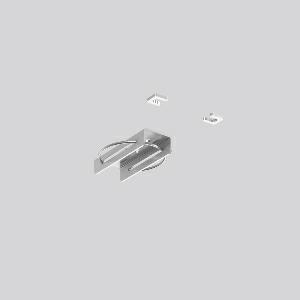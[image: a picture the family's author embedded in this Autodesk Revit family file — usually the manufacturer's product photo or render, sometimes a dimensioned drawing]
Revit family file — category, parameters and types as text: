
# Revit family: linedo_decke_adapter_982580_010_77cd
name_source: partatom
category: Lighting Fixtures
units: mm (PartAtom-declared; Revit-internal decimal feet)

## family parameters
Cut with Voids When Loaded = No
Host = Face
Light Source = No
Part Type = Normal
Room Calculation Point = No
Round Connector Dimension = Use Diameter
Shared = No

## types (1)
- LINEDO Decke Adapter
    Apparent Load = 0 VA
    Default Elevation = 1800 mm
    Description = Series: LINEDO
Adapter for direct ceiling installation. Galvanised sheet steel, for installing continuous line luminaire modules. Incl. 2 locking brackets.
Colour: unpainted
Length: 70 mm
Width: 28 mm
Height: 16 mm
Weight: 44 g
Type of Installation: Ceiling mounting
    Height = 16 mm
    Lamp = 0 x
    Length = 70 mm
    Luminous efficacy = 0 lm/W
    Manufacturer = RZB
    ModVariant = No
    Model = 982580.010
    Mounting Place = Ceiling
    Mounting Type = Surface mounted
    Number of Poles = 1
    OnlyDefault = Yes
    Power Factor = 1
    Product Name = LINEDO Decke Adapter
    Product group = Surface mounted continuous line luminaire system
    ProductGroupID = 310
    Protection Class = Protection class
    Protection Degree = Degree of protection
    RLX_Detail_Level = 1
    RLX_Emergency_Light_Flux = 0 lm
    RLX_Emergency_Type = 0
    RLX_Emergency_Type_DB = No
    RlxData = <blob elided: 9141 chars, md5=fc79c1e0>
    Standby Power = 0 W
    System Light Flux = 0 lm
    System Power = 0 W
    Type Comments = Product without accessories
    Type Image = 982580.010.jpg
    URL = http://relux.com
    VarID = ---
    Voltage = 0 V
    Weight = 0.00 kg
    Width = 28 mm

## geometry (parser evidence)
native form markers: Sweep x9
no freeform markers — native parametric forms only
